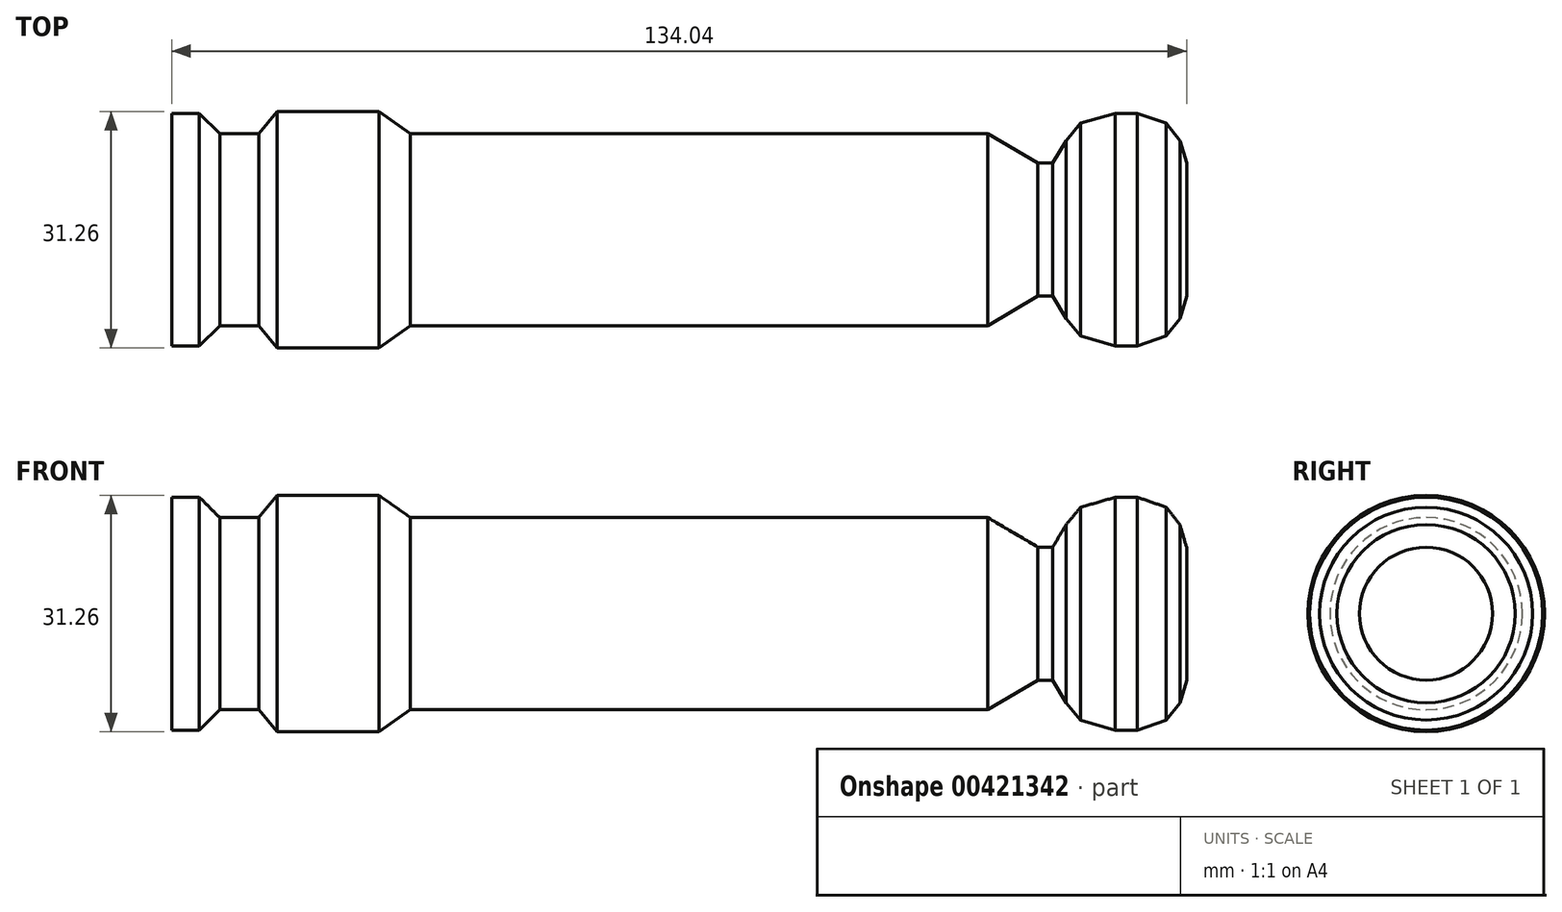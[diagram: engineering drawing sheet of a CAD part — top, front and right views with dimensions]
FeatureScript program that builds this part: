
annotation { "Feature Type Name" : "Feature", "Feature Type Description" : "" }
export const myFeature = defineFeature(function(context is Context, id is Id, definition is map)
    precondition{}
    {
        {
            var Q0;
            Q0=qCreatedBy(makeId("Front.planeOp"),FACE);
            var sketch = newSketch(context, id + "F0", { "sketchPlane" : qUnion([Q0])});
            skLineSegment(sketch, "E0", {"start": v(0, 12.7) * mm, "end": v(-25.32, 12.7) * mm});
            skLineSegment(sketch, "E1", {"start": v(-25.32, 12.7) * mm, "end": v(-29.48, 15.63) * mm});
            skLineSegment(sketch, "E2", {"start": v(-29.48, 15.63) * mm, "end": v(-42.92, 15.63) * mm});
            skLineSegment(sketch, "E3", {"start": v(-42.92, 15.63) * mm, "end": v(-45.37, 12.7) * mm});
            skLineSegment(sketch, "E4", {"start": v(-45.37, 12.7) * mm, "end": v(-50.5, 12.7) * mm});
            skLineSegment(sketch, "E5", {"start": v(-50.5, 12.7) * mm, "end": v(-53.19, 15.39) * mm});
            skLineSegment(sketch, "E6", {"start": v(-53.19, 15.39) * mm, "end": v(-56.85, 15.39) * mm});
            skLineSegment(sketch, "E7", {"start": v(-56.85, 15.39) * mm, "end": v(-56.85, 0) * mm});
            skLineSegment(sketch, "E8", {"start": v(0, 12.7) * mm, "end": v(50.94, 12.7) * mm});
            skLineSegment(sketch, "E9", {"start": v(50.94, 12.7) * mm, "end": v(57.54, 8.79) * mm});
            skLineSegment(sketch, "E10", {"start": v(57.54, 8.79) * mm, "end": v(59.5, 8.79) * mm});
            skLineSegment(sketch, "E11", {"start": v(59.5, 8.79) * mm, "end": v(61.29, 11.77) * mm});
            skLineSegment(sketch, "E12", {"start": v(61.29, 11.77) * mm, "end": v(63.2, 14.06) * mm});
            skLineSegment(sketch, "E13", {"start": v(63.2, 14.06) * mm, "end": v(67.78, 15.39) * mm});
            skLineSegment(sketch, "E14", {"start": v(67.78, 15.39) * mm, "end": v(70.7, 15.39) * mm});
            skLineSegment(sketch, "E15", {"start": v(70.7, 15.39) * mm, "end": v(74.52, 14.06) * mm});
            skLineSegment(sketch, "E16", {"start": v(74.52, 14.06) * mm, "end": v(76.3, 11.77) * mm});
            skLineSegment(sketch, "E17", {"start": v(76.3, 11.77) * mm, "end": v(77.19, 8.79) * mm});
            skLineSegment(sketch, "E18", {"start": v(77.19, 8.79) * mm, "end": v(77.19, 5.28) * mm});
            skLineSegment(sketch, "E19", {"start": v(77.19, 5.28) * mm, "end": v(77.19, 0) * mm});
            skLineSegment(sketch, "E20.MirrorCS", {"start": v(-25.32, -12.7) * mm, "end": v(-29.48, -15.63) * mm});
            skLineSegment(sketch, "E21.MirrorCS", {"start": v(-42.92, -15.63) * mm, "end": v(-45.37, -12.7) * mm});
            skLineSegment(sketch, "E22.MirrorCS", {"start": v(-45.37, -12.7) * mm, "end": v(-50.5, -12.7) * mm});
            skLineSegment(sketch, "E23.MirrorCS", {"start": v(-50.5, -12.7) * mm, "end": v(-53.19, -15.39) * mm});
            skLineSegment(sketch, "E24.MirrorCS", {"start": v(77.19, -8.79) * mm, "end": v(77.19, -5.28) * mm});
            skLineSegment(sketch, "E25.MirrorCS", {"start": v(76.3, -11.77) * mm, "end": v(77.19, -8.79) * mm});
            skLineSegment(sketch, "E26.MirrorCS", {"start": v(70.7, -15.39) * mm, "end": v(74.52, -14.06) * mm});
            skLineSegment(sketch, "E27.MirrorCS", {"start": v(67.78, -15.39) * mm, "end": v(70.7, -15.39) * mm});
            skLineSegment(sketch, "E28.MirrorCS", {"start": v(50.94, -12.7) * mm, "end": v(57.54, -8.79) * mm});
            skLineSegment(sketch, "E29.MirrorCS", {"start": v(61.29, -11.77) * mm, "end": v(63.2, -14.06) * mm});
            skLineSegment(sketch, "E30.MirrorCS", {"start": v(59.5, -8.79) * mm, "end": v(61.29, -11.77) * mm});
            skLineSegment(sketch, "E31.MirrorCS", {"start": v(-53.19, -15.39) * mm, "end": v(-56.85, -15.39) * mm});
            skLineSegment(sketch, "E32.MirrorCS", {"start": v(74.52, -14.06) * mm, "end": v(76.3, -11.77) * mm});
            skLineSegment(sketch, "E33.MirrorCS", {"start": v(63.2, -14.06) * mm, "end": v(67.78, -15.39) * mm});
            skLineSegment(sketch, "E34.MirrorCS", {"start": v(57.54, -8.79) * mm, "end": v(59.5, -8.79) * mm});
            skLineSegment(sketch, "E35.MirrorCS", {"start": v(0, -12.7) * mm, "end": v(-25.32, -12.7) * mm});
            skLineSegment(sketch, "E36.MirrorCS", {"start": v(-29.48, -15.63) * mm, "end": v(-42.92, -15.63) * mm});
            skLineSegment(sketch, "E37.MirrorCS", {"start": v(0, -12.7) * mm, "end": v(50.94, -12.7) * mm});
            skLineSegment(sketch, "E38.MirrorCS", {"start": v(-56.85, -15.39) * mm, "end": v(-56.85, 0) * mm});
            skLineSegment(sketch, "E39", {"start": v(77.19, 0) * mm, "end": v(77.19, -5.28) * mm});
            skLineSegment(sketch, "E40", {"start": v(-56.85, 0) * mm, "end": v(77.19, 0) * mm});
            skSolve(sketch);
        }
        {
            var Q0;
            Q0=makeQuery(id+"F0.imprint","IMPRINT",FACE,{"disambiguationData":[TD([[makeQuery(id+"F0.imprint","IMPRINT",EDGE,{"derivedFrom":sQuery(id+"F0.wireOp",EDGE,"E20.MirrorCS")}),-1.0]])]});
            var Q1;
            Q1=sQuery(id+"F0.wireOp",EDGE,"E40");
            revolve(context, id + "F1", {"entities" : qUnion([Q0]), "axis" : qUnion([Q1]), "revolveType" : RevolveType.FULL});
        }
    });
